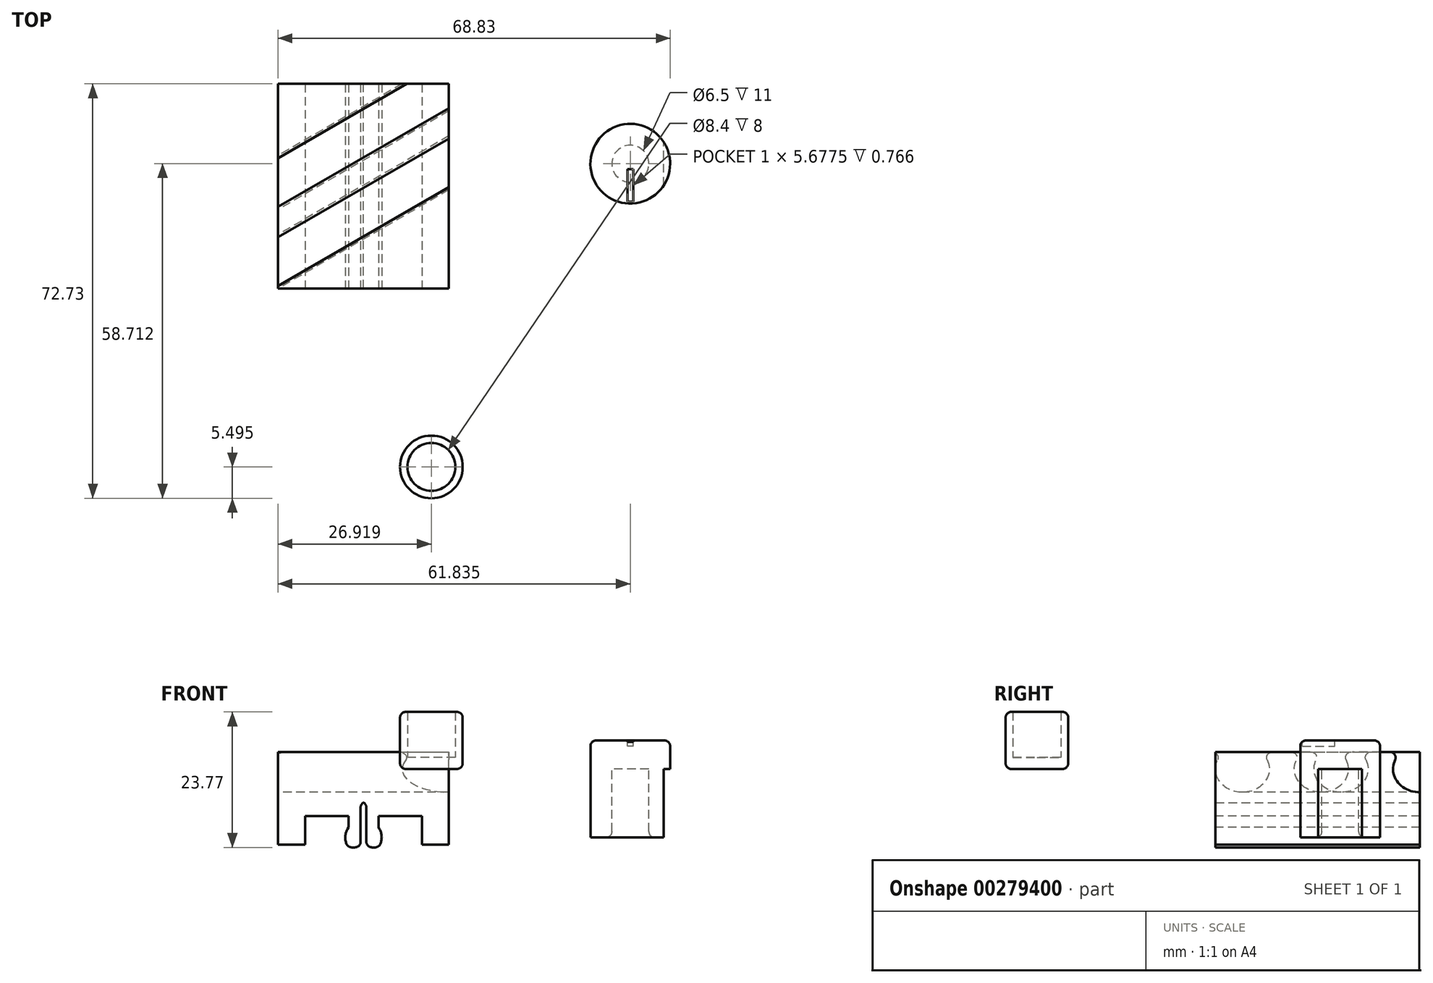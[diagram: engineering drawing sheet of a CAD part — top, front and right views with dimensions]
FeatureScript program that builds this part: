
annotation { "Feature Type Name" : "Feature", "Feature Type Description" : "" }
export const myFeature = defineFeature(function(context is Context, id is Id, definition is map)
    precondition{}
    {
        {
            var Q0;
            Q0=qCreatedBy(makeId("Top.planeOp"),FACE);
            var sketch = newSketch(context, id + "F0", { "sketchPlane" : qUnion([Q0])});
            skLineSegment(sketch, "E0.bottom", {"start": v(-28.83, 34.65) * mm, "end": v(1.17, 34.65) * mm});
            skLineSegment(sketch, "E0.top", {"start": v(-28.83, -1.26) * mm, "end": v(1.17, -1.26) * mm});
            skLineSegment(sketch, "E0.left", {"start": v(-28.83, 34.65) * mm, "end": v(-28.83, -1.26) * mm});
            skLineSegment(sketch, "E0.right", {"start": v(1.17, 34.65) * mm, "end": v(1.17, -1.26) * mm});
            skLineSegment(sketch, "E1", {"start": v(-42.48, 14.18) * mm, "end": v(0, 38.7) * mm});
            skLineSegment(sketch, "E2", {"start": v(0, 38.7) * mm, "end": v(2.05, 35.15) * mm});
            skLineSegment(sketch, "E3", {"start": v(2.05, 35.15) * mm, "end": v(-40.43, 10.63) * mm});
            skLineSegment(sketch, "E4", {"start": v(-40.43, 10.63) * mm, "end": v(-42.48, 14.18) * mm});
            skLineSegment(sketch, "E5", {"start": v(-28.83, 10.4) * mm, "end": v(1.17, 27.72) * mm});
            skLineSegment(sketch, "E6.MirrorCS", {"start": v(8.05, 24.76) * mm, "end": v(-34.43, 0.23) * mm});
            skLineSegment(sketch, "E7.MirrorCS", {"start": v(-32.38, -3.32) * mm, "end": v(10.1, 21.21) * mm});
            skLineSegment(sketch, "E8.MirrorCS", {"start": v(10.1, 21.21) * mm, "end": v(8.05, 24.76) * mm});
            skLineSegment(sketch, "E9.MirrorCS", {"start": v(-34.43, 0.23) * mm, "end": v(-32.38, -3.32) * mm});
            skSolve(sketch);
        }
        {
            var Q0;
            {var subQ0=sQuery(id+"F0.wireOp",EDGE,"E0.left");var subQ1=sQuery(id+"F0.wireOp",EDGE,"E0.bottom");var subQ2=makeQuery(id+"F0.imprint","INTERSECT",VERTEX,{"derivedFrom":[subQ1,subQ0]});Q0=makeQuery(id+"F0.imprint","IMPRINT",FACE,{"disambiguationData":[TD([[makeQuery(id+"F0.imprint","IMPRINT",EDGE,{"disambiguationData":[TD([[subQ2,-1.0]])],"derivedFrom":subQ1}),-1.0]])]});}
            var Q1;
            {var subQ3=sQuery(id+"F0.wireOp",EDGE,"E1");var subQ5=sQuery(id+"F0.wireOp",EDGE,"E0.left");var subQ6=makeQuery(id+"F0.imprint","INTERSECT",VERTEX,{"derivedFrom":[subQ5,subQ3]});Q1=makeQuery(id+"F0.imprint","IMPRINT",FACE,{"disambiguationData":[TD([[makeQuery(id+"F0.imprint","IMPRINT",EDGE,{"disambiguationData":[TD([[subQ6,-1.0]])],"derivedFrom":subQ5}),1.0]])]});}
            var Q2;
            {var subQ0=sQuery(id+"F0.wireOp",EDGE,"E5");Q2=makeQuery(id+"F0.imprint","IMPRINT",FACE,{"disambiguationData":[TD([[makeQuery(id+"F0.imprint","IMPRINT",EDGE,{"derivedFrom":subQ0}),1.0]])]});}
            var Q3;
            {var subQ0=sQuery(id+"F0.wireOp",EDGE,"E5");Q3=makeQuery(id+"F0.imprint","IMPRINT",FACE,{"disambiguationData":[TD([[makeQuery(id+"F0.imprint","IMPRINT",EDGE,{"derivedFrom":subQ0}),-1.0]])]});}
            var Q4;
            {var subQ0=sQuery(id+"F0.wireOp",EDGE,"E6.MirrorCS");var subQ1=sQuery(id+"F0.wireOp",EDGE,"E0.top");var subQ2=makeQuery(id+"F0.imprint","INTERSECT",VERTEX,{"derivedFrom":[subQ1,subQ0]});Q4=makeQuery(id+"F0.imprint","IMPRINT",FACE,{"disambiguationData":[TD([[makeQuery(id+"F0.imprint","IMPRINT",EDGE,{"disambiguationData":[TD([[subQ2,-1.0]])],"derivedFrom":subQ1}),1.0]])]});}
            var Q5;
            {var subQ0=sQuery(id+"F0.wireOp",EDGE,"E0.right");var subQ1=sQuery(id+"F0.wireOp",EDGE,"E0.top");var subQ2=makeQuery(id+"F0.imprint","INTERSECT",VERTEX,{"derivedFrom":[subQ1,subQ0]});Q5=makeQuery(id+"F0.imprint","IMPRINT",FACE,{"disambiguationData":[TD([[makeQuery(id+"F0.imprint","IMPRINT",EDGE,{"disambiguationData":[TD([[subQ2,1.0]])],"derivedFrom":subQ1}),1.0]])]});}
            var Q6;
            {var subQ3=sQuery(id+"F0.wireOp",EDGE,"E6.MirrorCS");var subQ5=sQuery(id+"F0.wireOp",EDGE,"E0.right");var subQ6=makeQuery(id+"F0.imprint","INTERSECT",VERTEX,{"derivedFrom":[subQ5,subQ3]});Q6=makeQuery(id+"F0.imprint","IMPRINT",FACE,{"disambiguationData":[TD([[makeQuery(id+"F0.imprint","IMPRINT",EDGE,{"disambiguationData":[TD([[subQ6,-1.0]])],"derivedFrom":subQ5}),-1.0]])]});}
            extrude(context, id + "F1", {"entities" : qUnion([Q0, Q1, Q2, Q3, Q4, Q5, Q6]), "oppositeDirection" : true, "depth" : 24 * mm, "hasSecondDirection" : true, "secondDirectionOppositeDirection" : false, "secondDirectionDepth" : 3 * mm});
        }
        {
            var Q0;
            {var subQ5=sQuery(id+"F0.wireOp",EDGE,"E4");Q0=makeQuery(id+"F0.imprint","IMPRINT",FACE,{"disambiguationData":[TD([[makeQuery(id+"F0.imprint","IMPRINT",EDGE,{"derivedFrom":subQ5}),-1.0]])]});}
            var Q1;
            {var subQ3=sQuery(id+"F0.wireOp",EDGE,"E1");var subQ5=sQuery(id+"F0.wireOp",EDGE,"E0.left");var subQ6=makeQuery(id+"F0.imprint","INTERSECT",VERTEX,{"derivedFrom":[subQ5,subQ3]});Q1=makeQuery(id+"F0.imprint","IMPRINT",FACE,{"disambiguationData":[TD([[makeQuery(id+"F0.imprint","IMPRINT",EDGE,{"disambiguationData":[TD([[subQ6,-1.0]])],"derivedFrom":subQ5}),1.0]])]});}
            var Q2;
            {var subQ5=sQuery(id+"F0.wireOp",EDGE,"E2");Q2=makeQuery(id+"F0.imprint","IMPRINT",FACE,{"disambiguationData":[TD([[makeQuery(id+"F0.imprint","IMPRINT",EDGE,{"derivedFrom":subQ5}),-1.0]])]});}
            var Q3;
            Q3=sQuery(id+"F0.wireOp",EDGE,"E3");
            revolve(context, id + "F2", {"operationType" : NewBodyOperationType.REMOVE, "entities" : qUnion([Q0, Q1, Q2]), "axis" : qUnion([Q3]), "revolveType" : RevolveType.FULL, "oppositeDirection" : true});
        }
        {
            var Q0;
            {var subQ5=sQuery(id+"F0.wireOp",EDGE,"E9.MirrorCS");Q0=makeQuery(id+"F0.imprint","IMPRINT",FACE,{"disambiguationData":[TD([[makeQuery(id+"F0.imprint","IMPRINT",EDGE,{"derivedFrom":subQ5}),1.0]])]});}
            var Q1;
            {var subQ3=sQuery(id+"F0.wireOp",EDGE,"E6.MirrorCS");var subQ5=sQuery(id+"F0.wireOp",EDGE,"E0.right");var subQ6=makeQuery(id+"F0.imprint","INTERSECT",VERTEX,{"derivedFrom":[subQ5,subQ3]});Q1=makeQuery(id+"F0.imprint","IMPRINT",FACE,{"disambiguationData":[TD([[makeQuery(id+"F0.imprint","IMPRINT",EDGE,{"disambiguationData":[TD([[subQ6,-1.0]])],"derivedFrom":subQ5}),-1.0]])]});}
            var Q2;
            {var subQ5=sQuery(id+"F0.wireOp",EDGE,"E8.MirrorCS");Q2=makeQuery(id+"F0.imprint","IMPRINT",FACE,{"disambiguationData":[TD([[makeQuery(id+"F0.imprint","IMPRINT",EDGE,{"derivedFrom":subQ5}),1.0]])]});}
            var Q3;
            Q3=sQuery(id+"F0.wireOp",EDGE,"E6.MirrorCS");
            revolve(context, id + "F3", {"operationType" : NewBodyOperationType.REMOVE, "entities" : qUnion([Q0, Q1, Q2]), "axis" : qUnion([Q3]), "revolveType" : RevolveType.FULL, "oppositeDirection" : true});
        }
        {
            var Q0;
            Q0=makeQuery(id+"F2.boolean.opBoolean","INTERSECT",EDGE,{"disambiguationData":[OD(0.0)],"derivedFrom":[makeQuery(id+"F1.opExtrude","CAP_FACE",FACE,{"disambiguationData":[OSD([sQuery(id+"F0.wireOp",EDGE,"E0.bottom"),sQuery(id+"F0.wireOp",EDGE,"E0.top"),sQuery(id+"F0.wireOp",EDGE,"E0.left"),sQuery(id+"F0.wireOp",EDGE,"E0.right")])],"isStart":true}),makeQuery(id+"F2.opRevolve","SWEPT_FACE",FACE,{"disambiguationData":[OSD([sQuery(id+"F0.wireOp",EDGE,"E1")])]})]});
            var Q1;
            Q1=makeQuery(id+"F2.boolean.opBoolean","INTERSECT",EDGE,{"disambiguationData":[OD(1.0)],"derivedFrom":[makeQuery(id+"F1.opExtrude","CAP_FACE",FACE,{"disambiguationData":[OSD([sQuery(id+"F0.wireOp",EDGE,"E0.bottom"),sQuery(id+"F0.wireOp",EDGE,"E0.top"),sQuery(id+"F0.wireOp",EDGE,"E0.left"),sQuery(id+"F0.wireOp",EDGE,"E0.right")])],"isStart":true}),makeQuery(id+"F2.opRevolve","SWEPT_FACE",FACE,{"disambiguationData":[OSD([sQuery(id+"F0.wireOp",EDGE,"E1")])]})]});
            var Q2;
            {var subQ0=sQuery(id+"F0.wireOp",EDGE,"E0.top");var subQ1=sQuery(id+"F0.wireOp",EDGE,"E0.left");var subQ2=sQuery(id+"F0.wireOp",EDGE,"E0.right");Q2=makeQuery(id+"F3.boolean.opBoolean","INTERSECT",EDGE,{"disambiguationData":[OD(0.0)],"derivedFrom":[makeQuery(id+"F2.boolean.opBoolean","SPLIT",FACE,{"disambiguationData":[TD([makeQuery(id+"F1.opExtrude","SWEPT_FACE",FACE,{"disambiguationData":[OSD([subQ0])]})])],"derivedFrom":makeQuery(id+"F1.opExtrude","CAP_FACE",FACE,{"disambiguationData":[OSD([sQuery(id+"F0.wireOp",EDGE,"E0.bottom"),subQ0,subQ1,subQ2])],"isStart":true})}),makeQuery(id+"F3.opRevolve","SWEPT_FACE",FACE,{"disambiguationData":[OSD([sQuery(id+"F0.wireOp",EDGE,"E7.MirrorCS")])]})]});}
            var Q3;
            {var subQ0=sQuery(id+"F0.wireOp",EDGE,"E0.top");var subQ1=sQuery(id+"F0.wireOp",EDGE,"E0.left");var subQ2=sQuery(id+"F0.wireOp",EDGE,"E0.right");Q3=makeQuery(id+"F3.boolean.opBoolean","INTERSECT",EDGE,{"disambiguationData":[OD(1.0)],"derivedFrom":[makeQuery(id+"F2.boolean.opBoolean","SPLIT",FACE,{"disambiguationData":[TD([makeQuery(id+"F1.opExtrude","SWEPT_FACE",FACE,{"disambiguationData":[OSD([subQ0])]})])],"derivedFrom":makeQuery(id+"F1.opExtrude","CAP_FACE",FACE,{"disambiguationData":[OSD([sQuery(id+"F0.wireOp",EDGE,"E0.bottom"),subQ0,subQ1,subQ2])],"isStart":true})}),makeQuery(id+"F3.opRevolve","SWEPT_FACE",FACE,{"disambiguationData":[OSD([sQuery(id+"F0.wireOp",EDGE,"E7.MirrorCS")])]})]});}
            fillet(context, id + "F4", {"entities" : qUnion([Q0, Q1, Q2, Q3]), "radius" : 1 * mm, "tangentPropagation" : true, "allowEdgeOverflow" : false});
        }
        {
            var Q0;
            Q0=makeQuery(id+"F1.opExtrude","SWEPT_FACE",FACE,{"disambiguationData":[OSD([sQuery(id+"F0.wireOp",EDGE,"E0.top")])]});
            var sketch = newSketch(context, id + "F5", { "sketchPlane" : qUnion([Q0])});
            skPoint(sketch, "E10.0", {"position": v(-28.83, -4.04) * mm});
            skLineSegment(sketch, "E11", {"start": v(-28.83, -8.27) * mm, "end": v(-16.48, -8.27) * mm});
            skLineSegment(sketch, "E12", {"start": v(-16.48, -8.27) * mm, "end": v(-16.48, -13.77) * mm});
            skLineSegment(sketch, "E13", {"start": v(-16.48, -13.77) * mm, "end": v(-11.18, -13.77) * mm});
            skLineSegment(sketch, "E14", {"start": v(-11.18, -13.77) * mm, "end": v(-11.18, -8.27) * mm});
            skLineSegment(sketch, "E15", {"start": v(-11.18, -8.27) * mm, "end": v(1.17, -8.27) * mm});
            skLineSegment(sketch, "E16", {"start": v(-16.48, -13.77) * mm, "end": v(-17.48, -12.02) * mm});
            skLineSegment(sketch, "E17", {"start": v(-17.48, -12.02) * mm, "end": v(-16.48, -10.27) * mm});
            skLineSegment(sketch, "E18", {"start": v(-13.83, -13.77) * mm, "end": v(-13.83, -8.27) * mm, "construction": true});
            skLineSegment(sketch, "E19.MirrorCS", {"start": v(-10.18, -12.02) * mm, "end": v(-11.18, -10.27) * mm});
            skLineSegment(sketch, "E20.MirrorCS", {"start": v(-11.18, -13.77) * mm, "end": v(-10.18, -12.02) * mm});
            skLineSegment(sketch, "E21", {"start": v(-14.33, -13.77) * mm, "end": v(-14.33, -5.77) * mm});
            skLineSegment(sketch, "E22", {"start": v(-14.33, -5.77) * mm, "end": v(-13.33, -5.77) * mm});
            skLineSegment(sketch, "E23", {"start": v(-13.33, -5.77) * mm, "end": v(-13.33, -13.77) * mm});
            skLineSegment(sketch, "E24", {"start": v(-24.08, -8.27) * mm, "end": v(-24.08, -13.27) * mm});
            skLineSegment(sketch, "E25", {"start": v(-24.08, -13.27) * mm, "end": v(-28.83, -8.27) * mm, "construction": true});
            skLineSegment(sketch, "E26.MirrorCS", {"start": v(-3.58, -8.27) * mm, "end": v(-3.58, -13.27) * mm});
            skLineSegment(sketch, "E27.MirrorCS", {"start": v(-3.58, -13.27) * mm, "end": v(1.17, -8.27) * mm, "construction": true});
            skLineSegment(sketch, "E28", {"start": v(-16.48, -8.27) * mm, "end": v(-16.48, -5.77) * mm});
            skLineSegment(sketch, "E29", {"start": v(-16.48, -5.77) * mm, "end": v(-15.41, -8.27) * mm});
            skLineSegment(sketch, "E30.MirrorCS", {"start": v(-11.18, -8.27) * mm, "end": v(-11.18, -5.77) * mm});
            skLineSegment(sketch, "E31.MirrorCS", {"start": v(-11.18, -5.77) * mm, "end": v(-12.24, -8.27) * mm});
            skLineSegment(sketch, "E32", {"start": v(-24.08, -13.27) * mm, "end": v(-28.83, -13.27) * mm});
            skLineSegment(sketch, "E33", {"start": v(-3.58, -13.27) * mm, "end": v(1.17, -13.27) * mm});
            skSolve(sketch);
        }
        {
            var Q0;
            {var subQ0=sQuery(id+"F5.wireOp",EDGE,"E16");Q0=makeQuery(id+"F5.imprint","IMPRINT",FACE,{"disambiguationData":[TD([[makeQuery(id+"F5.imprint","IMPRINT",EDGE,{"derivedFrom":subQ0}),1.0]])]});}
            var Q1;
            {var subQ0=sQuery(id+"F5.wireOp",EDGE,"E21");Q1=makeQuery(id+"F5.imprint","IMPRINT",FACE,{"disambiguationData":[TD([[makeQuery(id+"F5.imprint","IMPRINT",EDGE,{"derivedFrom":subQ0}),-1.0]])]});}
            var Q2;
            {var subQ0=sQuery(id+"F5.wireOp",EDGE,"E28");Q2=makeQuery(id+"F5.imprint","IMPRINT",FACE,{"disambiguationData":[TD([[makeQuery(id+"F5.imprint","IMPRINT",EDGE,{"derivedFrom":subQ0}),1.0]])]});}
            var Q3;
            {var subQ0=sQuery(id+"F5.wireOp",EDGE,"E30.MirrorCS");Q3=makeQuery(id+"F5.imprint","IMPRINT",FACE,{"disambiguationData":[TD([[makeQuery(id+"F5.imprint","IMPRINT",EDGE,{"derivedFrom":subQ0}),-1.0]])]});}
            extrude(context, id + "F6", {"entities" : qUnion([Q0, Q1, Q2, Q3]), "operationType" : NewBodyOperationType.REMOVE, "oppositeDirection" : true, "depth" : 43.7 * mm});
        }
        {
            var Q0;
            Q0=makeQuery(id+"F6.boolean.opBoolean","COPY",EDGE,{"derivedFrom":makeQuery(id+"F6.opExtrude","SWEPT_EDGE",EDGE,{"disambiguationData":[OSD([sQuery(id+"F5.wireOp",EDGE,"E16"),sQuery(id+"F5.wireOp",EDGE,"E17")])]})});
            var Q1;
            Q1=makeQuery(id+"F6.boolean.opBoolean","COPY",EDGE,{"derivedFrom":makeQuery(id+"F6.opExtrude","SWEPT_EDGE",EDGE,{"disambiguationData":[OSD([sQuery(id+"F5.wireOp",EDGE,"E19.MirrorCS"),sQuery(id+"F5.wireOp",EDGE,"E20.MirrorCS")])]})});
            fillet(context, id + "F7", {"entities" : qUnion([Q0, Q1]), "radius" : 3 * mm, "tangentPropagation" : true, "allowEdgeOverflow" : false});
        }
        {
            var Q0;
            Q0=makeQuery(id+"F6.boolean.opBoolean","COPY",EDGE,{"derivedFrom":makeQuery(id+"F6.opExtrude","SWEPT_EDGE",EDGE,{"disambiguationData":[OSD([sQuery(id+"F5.wireOp",EDGE,"E13"),sQuery(id+"F5.wireOp",EDGE,"E21")])]})});
            var Q1;
            Q1=makeQuery(id+"F6.boolean.opBoolean","COPY",EDGE,{"derivedFrom":makeQuery(id+"F6.opExtrude","SWEPT_EDGE",EDGE,{"disambiguationData":[OSD([sQuery(id+"F5.wireOp",EDGE,"E12"),sQuery(id+"F5.wireOp",EDGE,"E13"),sQuery(id+"F5.wireOp",EDGE,"E16")])]})});
            var Q2;
            Q2=makeQuery(id+"F6.boolean.opBoolean","COPY",EDGE,{"derivedFrom":makeQuery(id+"F6.opExtrude","SWEPT_EDGE",EDGE,{"disambiguationData":[OSD([sQuery(id+"F5.wireOp",EDGE,"E13"),sQuery(id+"F5.wireOp",EDGE,"E23")])]})});
            var Q3;
            Q3=makeQuery(id+"F6.boolean.opBoolean","COPY",EDGE,{"derivedFrom":makeQuery(id+"F6.opExtrude","SWEPT_EDGE",EDGE,{"disambiguationData":[OSD([sQuery(id+"F5.wireOp",EDGE,"E13"),sQuery(id+"F5.wireOp",EDGE,"E14"),sQuery(id+"F5.wireOp",EDGE,"E20.MirrorCS")])]})});
            var Q4;
            Q4=makeQuery(id+"F6.boolean.opBoolean","COPY",EDGE,{"derivedFrom":makeQuery(id+"F6.opExtrude","SWEPT_EDGE",EDGE,{"disambiguationData":[OSD([sQuery(id+"F5.wireOp",EDGE,"E22"),sQuery(id+"F5.wireOp",EDGE,"E23")])]})});
            var Q5;
            Q5=makeQuery(id+"F6.boolean.opBoolean","COPY",EDGE,{"derivedFrom":makeQuery(id+"F6.opExtrude","SWEPT_EDGE",EDGE,{"disambiguationData":[OSD([sQuery(id+"F5.wireOp",EDGE,"E21"),sQuery(id+"F5.wireOp",EDGE,"E22")])]})});
            fillet(context, id + "F8", {"entities" : qUnion([Q0, Q1, Q2, Q3, Q4, Q5]), "radius" : 1 * mm, "tangentPropagation" : true, "allowEdgeOverflow" : false});
        }
        {
            var Q0;
            Q0=qCreatedBy(makeId("Top.planeOp"),FACE);
            var sketch = newSketch(context, id + "F9", { "sketchPlane" : qUnion([Q0])});
            skCircle(sketch, "E34", {"center": v(33, 20.63) * mm, "radius": 3.25 * mm});
            skCircle(sketch, "E35", {"center": v(33, 20.63) * mm, "radius": 7 * mm});
            skLineSegment(sketch, "E36", {"start": v(38.87, 16.8) * mm, "end": v(38.87, 24.46) * mm});
            skSolve(sketch);
        }
        {
            var Q0;
            Q0=makeQuery(id+"F9.imprint","IMPRINT",FACE,{"disambiguationData":[TD([[makeQuery(id+"F9.imprint","IMPRINT",EDGE,{"derivedFrom":sQuery(id+"F9.wireOp",EDGE,"E34")}),-1.0]])]});
            var Q1;
            Q1=makeQuery(id+"F9.imprint","IMPRINT",FACE,{"disambiguationData":[TD([[makeQuery(id+"F9.imprint","IMPRINT",EDGE,{"derivedFrom":sQuery(id+"F9.wireOp",EDGE,"E34")}),1.0]])]});
            var Q2;
            {var subQ0=sQuery(id+"F9.wireOp",EDGE,"E36");Q2=makeQuery(id+"F9.imprint","IMPRINT",FACE,{"disambiguationData":[TD([[makeQuery(id+"F9.imprint","IMPRINT",EDGE,{"derivedFrom":subQ0}),-1.0]])]});}
            extrude(context, id + "F10", {"entities" : qUnion([Q0, Q1, Q2]), "depth" : 5 * mm});
        }
        {
            var Q0;
            Q0=makeQuery(id+"F9.imprint","IMPRINT",FACE,{"disambiguationData":[TD([[makeQuery(id+"F9.imprint","IMPRINT",EDGE,{"derivedFrom":sQuery(id+"F9.wireOp",EDGE,"E34")}),-1.0]])]});
            extrude(context, id + "F11", {"entities" : qUnion([Q0]), "operationType" : NewBodyOperationType.ADD, "oppositeDirection" : true, "depth" : 12 * mm});
        }
        {
            var Q0;
            Q0=makeQuery(id+"F11.opExtrude","SWEPT_FACE",FACE,{"disambiguationData":[OSD([sQuery(id+"F9.wireOp",EDGE,"E36")])]});
            var sketch = newSketch(context, id + "F12", { "sketchPlane" : qUnion([Q0])});
            skCircle(sketch, "E37", {"center": v(20.63, -6) * mm, "radius": 2.08 * mm});
            skPoint(sketch, "E37.centerSnap0", {"position": v(24.46, -6) * mm});
            skPoint(sketch, "E37.centerSnap1", {"position": v(20.63, -12) * mm});
            skSolve(sketch);
        }
        {
            var Q0;
            Q0=makeQuery(id+"F10.opExtrude","CAP_FACE",FACE,{"disambiguationData":[OSD([sQuery(id+"F9.wireOp",EDGE,"E35")])],"isStart":false});
            var sketch = newSketch(context, id + "F13", { "sketchPlane" : qUnion([Q0])});
            skLineSegment(sketch, "E38.bottom", {"start": v(33.5, 13.99) * mm, "end": v(32.5, 13.99) * mm});
            skLineSegment(sketch, "E38.top", {"start": v(33.5, 19.67) * mm, "end": v(32.5, 19.67) * mm});
            skLineSegment(sketch, "E38.left", {"start": v(33.5, 13.99) * mm, "end": v(33.5, 19.67) * mm});
            skLineSegment(sketch, "E38.right", {"start": v(32.5, 13.99) * mm, "end": v(32.5, 19.67) * mm});
            skPoint(sketch, "E38.middle", {"position": v(33, 16.83) * mm});
            skSolve(sketch);
        }
        {
            var Q0;
            {var subQ0=sQuery(id+"F13.wireOp",EDGE,"E38.top");Q0=makeQuery(id+"F13.imprint","IMPRINT",FACE,{"disambiguationData":[TD([[makeQuery(id+"F13.imprint","IMPRINT",EDGE,{"derivedFrom":subQ0}),1.0]])]});}
            extrude(context, id + "F14", {"entities" : qUnion([Q0]), "operationType" : NewBodyOperationType.REMOVE, "oppositeDirection" : true, "depth" : 1 * mm});
        }
        {
            var Q0;
            Q0=makeQuery(id+"F10.opExtrude","CAP_EDGE",EDGE,{"disambiguationData":[OSD([sQuery(id+"F9.wireOp",EDGE,"E35")])],"isStart":false});
            var Q1;
            Q1=makeQuery(id+"FrH1lP31orcuvX2_2.hole-0.boolean.opBoolean","COPY",EDGE,{"derivedFrom":makeQuery(id+"FrH1lP31orcuvX2_2.hole-0.opRevolve","SWEPT_EDGE",EDGE,{"disambiguationData":[OSD([sQuery(id+"FrH1lP31orcuvX2_2.hole-0.sketch.wireOp",EDGE,"cbore_start_line_2"),sQuery(id+"FrH1lP31orcuvX2_2.hole-0.sketch.wireOp",EDGE,"cbore_start_line_3")])]})});
            var Q2;
            Q2=makeQuery(id+"F11.opExtrude","CAP_EDGE",EDGE,{"disambiguationData":[OSD([sQuery(id+"F9.wireOp",EDGE,"E34")])],"isStart":false});
            fillet(context, id + "F15", {"entities" : qUnion([Q0, Q1, Q2]), "radius" : 1 * mm, "tangentPropagation" : true, "allowEdgeOverflow" : false});
        }
        {
            var Q0;
            Q0=qCreatedBy(makeId("Top.planeOp"),FACE);
            var sketch = newSketch(context, id + "F16", { "sketchPlane" : qUnion([Q0])});
            skCircle(sketch, "E39", {"center": v(-1.91, -32.58) * mm, "radius": 4.2 * mm});
            skCircle(sketch, "E40", {"center": v(-1.91, -32.58) * mm, "radius": 5.5 * mm});
            skSolve(sketch);
        }
        {
            var Q0;
            Q0=makeQuery(id+"F16.imprint","IMPRINT",FACE,{"disambiguationData":[TD([[makeQuery(id+"F16.imprint","IMPRINT",EDGE,{"derivedFrom":sQuery(id+"F16.wireOp",EDGE,"E39")}),-1.0]])]});
            extrude(context, id + "F17", {"entities" : qUnion([Q0]), "depth" : 10 * mm});
        }
        {
            var Q0;
            Q0=makeQuery(id+"F16.imprint","IMPRINT",FACE,{"disambiguationData":[TD([[makeQuery(id+"F16.imprint","IMPRINT",EDGE,{"derivedFrom":sQuery(id+"F16.wireOp",EDGE,"E39")}),1.0]])]});
            extrude(context, id + "F18", {"entities" : qUnion([Q0]), "operationType" : NewBodyOperationType.ADD, "depth" : 2 * mm});
        }
        {
            var Q0;
            Q0=makeQuery(id+"F17.opExtrude","CAP_EDGE",EDGE,{"disambiguationData":[OSD([sQuery(id+"F16.wireOp",EDGE,"E40")])],"isStart":true});
            var Q1;
            Q1=makeQuery(id+"F17.opExtrude","CAP_EDGE",EDGE,{"disambiguationData":[OSD([sQuery(id+"F16.wireOp",EDGE,"E40")])],"isStart":false});
            fillet(context, id + "F19", {"entities" : qUnion([Q0, Q1]), "radius" : 1 * mm, "tangentPropagation" : true, "allowEdgeOverflow" : false});
        }
    });
